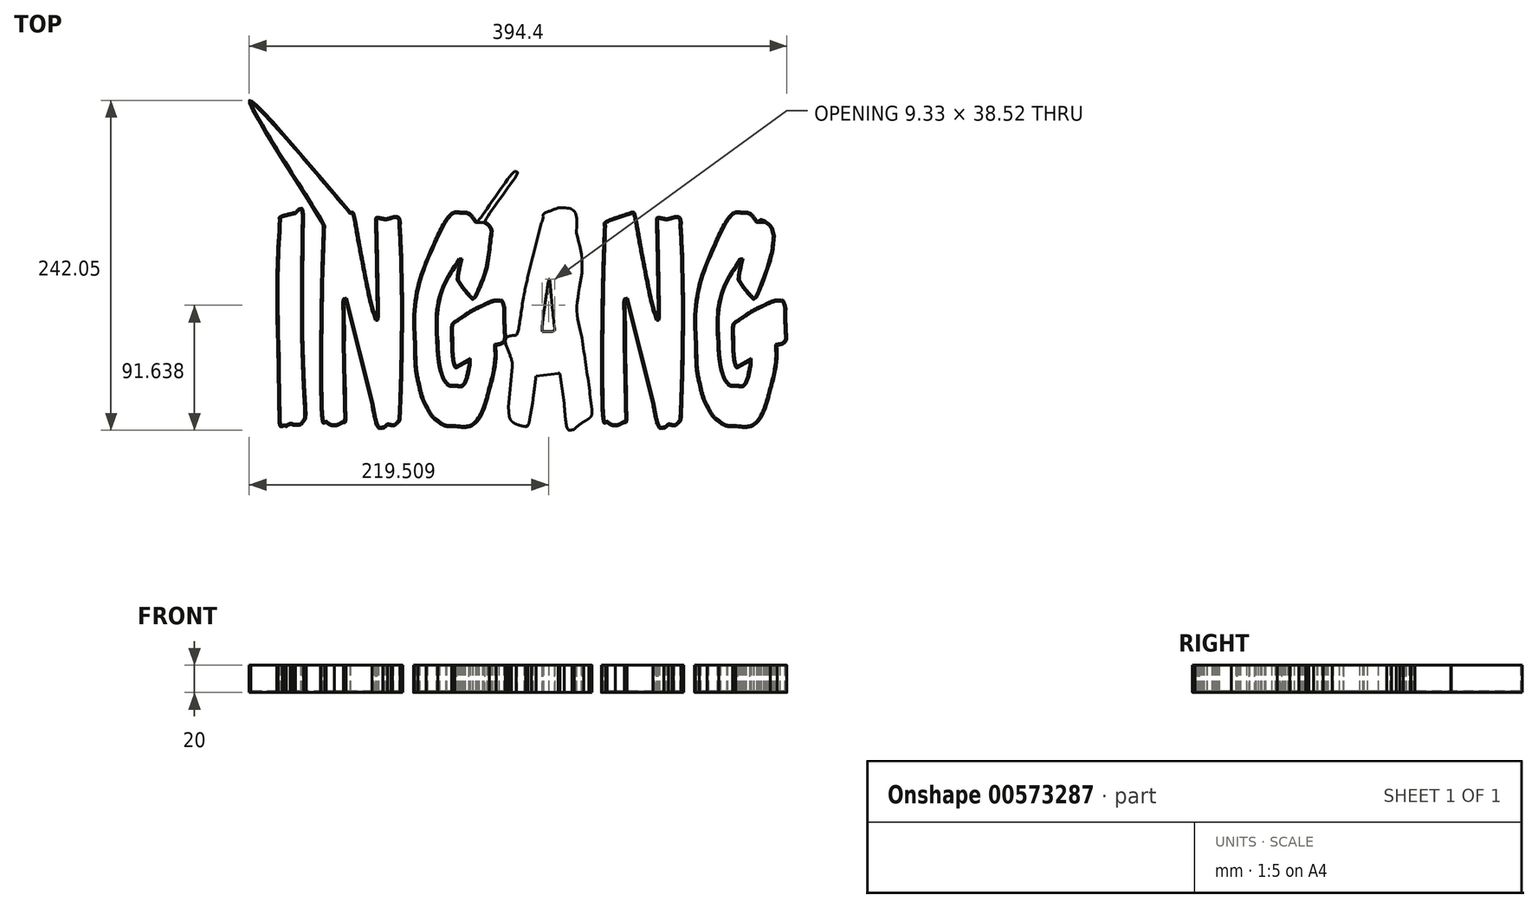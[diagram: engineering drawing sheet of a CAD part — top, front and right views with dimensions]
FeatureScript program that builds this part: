
annotation { "Feature Type Name" : "Feature", "Feature Type Description" : "" }
export const myFeature = defineFeature(function(context is Context, id is Id, definition is map)
    precondition{}
    {
        {
            var Q0;
            Q0=qCreatedBy(makeId("Top.planeOp"),FACE);
            var sketch = newSketch(context, id + "F0", { "sketchPlane" : qUnion([Q0])});
            skFitSpline(sketch, "E0", {"points": [v(-169.64, 100.47) * mm, v(-168.45, 100.47) * mm, v(-167.69, 98.57) * mm, v(-167.37, 94.75) * mm]});
            skFitSpline(sketch, "E1", {"points": [v(-167.37, 94.75) * mm, v(-167.69, 74.14) * mm, v(-167.89, 56.43) * mm, v(-167.97, 41.62) * mm]});
            skFitSpline(sketch, "E2", {"points": [v(-167.97, 41.62) * mm, v(-168.05, 26.8) * mm, v(-168, 14.37) * mm, v(-167.85, 4.29) * mm]});
            skFitSpline(sketch, "E3", {"points": [v(-167.85, 4.29) * mm, v(-167.69, -2.12) * mm, v(-167.45, -9.53) * mm, v(-167.13, -17.92) * mm]});
            skFitSpline(sketch, "E4", {"points": [v(-167.13, -17.92) * mm, v(-166.8, -26.32) * mm, v(-166.33, -35.86) * mm, v(-165.7, -46.55) * mm]});
            skFitSpline(sketch, "E5", {"points": [v(-165.7, -46.55) * mm, v(-165.61, -51.28) * mm, v(-166.21, -54.5) * mm, v(-167.49, -56.17) * mm]});
            skFitSpline(sketch, "E6", {"points": [v(-167.49, -56.17) * mm, v(-168.76, -57.85) * mm, v(-170.72, -58.69) * mm, v(-173.36, -58.69) * mm]});
            skFitSpline(sketch, "E7", {"points": [v(-173.36, -58.69) * mm, v(-174.15, -58.69) * mm, v(-174.87, -58.61) * mm, v(-175.51, -58.46) * mm]});
            skFitSpline(sketch, "E8", {"points": [v(-175.51, -58.46) * mm, v(-176.15, -58.15) * mm, v(-176.7, -58.08) * mm, v(-177.19, -58.23) * mm]});
            skFitSpline(sketch, "E9", {"points": [v(-177.19, -58.23) * mm, v(-177.59, -58.23) * mm, v(-178.5, -58.69) * mm, v(-179.94, -59.6) * mm]});
            skFitSpline(sketch, "E10", {"points": [v(-182.94, -59.6) * mm, v(-184.53, -59.6) * mm, v(-185.45, -54.41) * mm, v(-185.7, -44.03) * mm]});
            skLineSegment(sketch, "E11", {"start": v(-179.94, -59.6) * mm, "end": v(-181.38, -59.15) * mm});
            skLineSegment(sketch, "E12", {"start": v(-181.38, -59.15) * mm, "end": v(-182.94, -59.6) * mm});
            skFitSpline(sketch, "E13", {"points": [v(-186.17, -11.74) * mm, v(-187.05, 27.95) * mm, v(-186.69, 62.69) * mm, v(-185.1, 92.46) * mm]});
            skFitSpline(sketch, "E14", {"points": [v(-185.1, 92.46) * mm, v(-185.25, 93.99) * mm, v(-181.38, 95.74) * mm, v(-173.48, 97.73) * mm]});
            skFitSpline(sketch, "E15", {"points": [v(-173.48, 97.73) * mm, v(-171.72, 99.56) * mm, v(-170.44, 100.47) * mm, v(-169.64, 100.47) * mm]});
            skLineSegment(sketch, "E16", {"start": v(-185.7, -44.03) * mm, "end": v(-186.17, -11.74) * mm});
            skFitSpline(sketch, "E17", {"points": [v(-132.92, 97.73) * mm, v(-131.25, 97.73) * mm, v(-128.53, 87.42) * mm, v(-124.78, 66.8) * mm]});
            skFitSpline(sketch, "E18", {"points": [v(-124.78, 66.8) * mm, v(-120.07, 42.69) * mm, v(-116.43, 26.89) * mm, v(-113.88, 19.4) * mm]});
            skFitSpline(sketch, "E19", {"points": [v(-113.64, 19.4) * mm, v(-113.48, 23.98) * mm, v(-113.48, 30.1) * mm, v(-113.64, 37.72) * mm]});
            skFitSpline(sketch, "E20", {"points": [v(-113.64, 37.72) * mm, v(-113.72, 42.46) * mm, v(-113.84, 49.18) * mm, v(-114, 57.88) * mm]});
            skFitSpline(sketch, "E21", {"points": [v(-114, 57.88) * mm, v(-114.16, 66.73) * mm, v(-114.4, 77.88) * mm, v(-114.72, 91.31) * mm]});
            skFitSpline(sketch, "E22", {"points": [v(-114.72, 91.31) * mm, v(-114.64, 93.15) * mm, v(-113.84, 94.06) * mm, v(-112.32, 94.06) * mm]});
            skFitSpline(sketch, "E23", {"points": [v(-112.32, 94.06) * mm, v(-110.97, 93.76) * mm, v(-109.93, 93.53) * mm, v(-109.2, 93.37) * mm]});
            skFitSpline(sketch, "E24", {"points": [v(-109.2, 93.37) * mm, v(-108.41, 93.22) * mm, v(-107.93, 93.15) * mm, v(-107.77, 93.15) * mm]});
            skLineSegment(sketch, "E25", {"start": v(-113.88, 19.4) * mm, "end": v(-113.64, 19.4) * mm});
            skFitSpline(sketch, "E26", {"points": [v(-107.05, 93.15) * mm, v(-106.57, 93.15) * mm, v(-104.82, 93.6) * mm, v(-101.78, 94.52) * mm]});
            skFitSpline(sketch, "E27", {"points": [v(-101.78, 94.52) * mm, v(-98.35, 94.52) * mm, v(-96.6, 92.15) * mm, v(-96.51, 87.42) * mm]});
            skFitSpline(sketch, "E28", {"points": [v(-96.51, 87.42) * mm, v(-96.2, 83.15) * mm, v(-95.96, 78.72) * mm, v(-95.8, 74.14) * mm]});
            skFitSpline(sketch, "E29", {"points": [v(-95.8, 74.14) * mm, v(-95.56, 69.71) * mm, v(-95.36, 65.13) * mm, v(-95.2, 60.4) * mm]});
            skLineSegment(sketch, "E30", {"start": v(-107.77, 93.15) * mm, "end": v(-107.05, 93.15) * mm});
            skFitSpline(sketch, "E31", {"points": [v(-94.96, 45.74) * mm, v(-94.72, 31.85) * mm, v(-94.72, 16.58) * mm, v(-94.96, -0.06) * mm]});
            skFitSpline(sketch, "E32", {"points": [v(-94.96, -0.06) * mm, v(-95.2, -16.55) * mm, v(-95.72, -34.8) * mm, v(-96.51, -54.8) * mm]});
            skFitSpline(sketch, "E33", {"points": [v(-96.51, -54.8) * mm, v(-98.83, -57.54) * mm, v(-100.7, -58.92) * mm, v(-102.14, -58.92) * mm]});
            skLineSegment(sketch, "E34", {"start": v(-95.2, 60.4) * mm, "end": v(-94.96, 45.74) * mm});
            skFitSpline(sketch, "E35", {"points": [v(-103.34, -58.92) * mm, v(-103.9, -58.76) * mm, v(-104.7, -58.61) * mm, v(-105.74, -58.46) * mm]});
            skFitSpline(sketch, "E36", {"points": [v(-105.74, -58.46) * mm, v(-107.41, -59.99) * mm, v(-108.57, -60.75) * mm, v(-109.2, -60.75) * mm]});
            skFitSpline(sketch, "E37", {"points": [v(-109.2, -60.75) * mm, v(-112.32, -60.75) * mm, v(-115.04, -55.1) * mm, v(-117.35, -43.8) * mm]});
            skLineSegment(sketch, "E38", {"start": v(-102.14, -58.92) * mm, "end": v(-103.34, -58.92) * mm});
            skFitSpline(sketch, "E39", {"points": [v(-136.87, 33.6) * mm, v(-137.35, 33.6) * mm, v(-137.51, 23.07) * mm, v(-137.35, 2) * mm]});
            skLineSegment(sketch, "E40", {"start": v(-117.35, -43.8) * mm, "end": v(-136.63, 33.6) * mm});
            skLineSegment(sketch, "E41", {"start": v(-136.63, 33.6) * mm, "end": v(-136.87, 33.6) * mm});
            skFitSpline(sketch, "E42", {"points": [v(-136.75, -28.46) * mm, v(-136.43, -47.24) * mm, v(-136.95, -56.63) * mm, v(-138.31, -56.63) * mm]});
            skFitSpline(sketch, "E43", {"points": [v(-138.31, -56.63) * mm, v(-141.03, -58.15) * mm, v(-143.18, -58.92) * mm, v(-144.78, -58.92) * mm]});
            skFitSpline(sketch, "E44", {"points": [v(-144.78, -58.92) * mm, v(-146.93, -58.92) * mm, v(-148.93, -58.15) * mm, v(-150.77, -56.63) * mm]});
            skLineSegment(sketch, "E45", {"start": v(-137.35, 2) * mm, "end": v(-136.75, -28.46) * mm});
            skFitSpline(sketch, "E46", {"points": [v(-151.72, -57.09) * mm, v(-153.08, -57.09) * mm, v(-154.04, -53.65) * mm, v(-154.6, -46.78) * mm]});
            skFitSpline(sketch, "E47", {"points": [v(-154.6, -46.78) * mm, v(-155, -25.1) * mm, v(-155.04, -3.34) * mm, v(-154.72, 18.49) * mm]});
            skFitSpline(sketch, "E48", {"points": [v(-154.72, 18.49) * mm, v(-154.4, 40.47) * mm, v(-153.8, 63.45) * mm, v(-152.92, 87.42) * mm]});
            skFitSpline(sketch, "E49", {"points": [v(-152.92, 87.42) * mm, v(-153.43, 89.02) * mm, v(-207.01, 177.85) * mm, v(-132.92, 97.73) * mm]});
            skLineSegment(sketch, "E50", {"start": v(-150.77, -56.63) * mm, "end": v(-151.72, -57.09) * mm});
            skFitSpline(sketch, "E51", {"points": [v(-50.81, 97.73) * mm, v(-47.46, 97.73) * mm, v(-44.15, 95.51) * mm, v(-40.87, 91.08) * mm]});
            skFitSpline(sketch, "E52", {"points": [v(-40.4, 91.08) * mm, v(-38.96, 92) * mm, v(-12.73, 127.61) * mm, v(-11.56, 127.23) * mm]});
            skFitSpline(sketch, "E53", {"points": [v(-11.56, 127.23) * mm, v(-10.4, 126.85) * mm, v(-34.2, 90.86) * mm, v(-33.09, 89.94) * mm]});
            skFitSpline(sketch, "E54", {"points": [v(-33.09, 89.94) * mm, v(-31.9, 89.18) * mm, v(-30.97, 88.26) * mm, v(-30.33, 87.2) * mm]});
            skFitSpline(sketch, "E55", {"points": [v(-30.33, 87.2) * mm, v(-29.7, 86.28) * mm, v(-29.26, 85.2) * mm, v(-29.02, 83.99) * mm]});
            skFitSpline(sketch, "E56", {"points": [v(-29.02, 83.99) * mm, v(-30.3, 73.15) * mm, v(-32.93, 56.12) * mm, v(-38.84, 40.24) * mm]});
            skFitSpline(sketch, "E57", {"points": [v(-38.84, 40.24) * mm, v(-40.35, 36.89) * mm, v(-41.8, 34.75) * mm, v(-43.15, 33.83) * mm]});
            skFitSpline(sketch, "E58", {"points": [v(-43.15, 33.83) * mm, v(-43.63, 33.83) * mm, v(-44.5, 34.52) * mm, v(-45.78, 35.9) * mm]});
            skFitSpline(sketch, "E59", {"points": [v(-45.78, 35.9) * mm, v(-47.06, 37.27) * mm, v(-48.38, 38.8) * mm, v(-49.73, 40.47) * mm]});
            skFitSpline(sketch, "E60", {"points": [v(-49.73, 40.47) * mm, v(-51.1, 42.15) * mm, v(-52.29, 43.83) * mm, v(-53.33, 45.51) * mm]});
            skFitSpline(sketch, "E61", {"points": [v(-53.33, 45.51) * mm, v(-54.37, 47.2) * mm, v(-54.88, 48.26) * mm, v(-54.88, 48.72) * mm]});
            skFitSpline(sketch, "E62", {"points": [v(-54.88, 48.72) * mm, v(-54.57, 51.92) * mm, v(-53.73, 56.5) * mm, v(-52.37, 62.46) * mm]});
            skLineSegment(sketch, "E63", {"start": v(-40.87, 91.08) * mm, "end": v(-40.4, 91.08) * mm});
            skFitSpline(sketch, "E64", {"points": [v(-52.85, 62.46) * mm, v(-63.79, 44.29) * mm, v(-69.02, 23.3) * mm, v(-68.54, -0.52) * mm]});
            skFitSpline(sketch, "E65", {"points": [v(-68.54, -0.52) * mm, v(-68.46, -4.18) * mm, v(-68.18, -7.77) * mm, v(-67.7, -11.28) * mm]});
            skFitSpline(sketch, "E66", {"points": [v(-67.7, -11.28) * mm, v(-67.22, -14.64) * mm, v(-66.58, -17.7) * mm, v(-65.78, -20.44) * mm]});
            skFitSpline(sketch, "E67", {"points": [v(-65.78, -20.44) * mm, v(-64.9, -23.04) * mm, v(-63.83, -25.18) * mm, v(-62.55, -26.86) * mm]});
            skFitSpline(sketch, "E68", {"points": [v(-62.55, -26.86) * mm, v(-61.27, -28.38) * mm, v(-59.75, -29.15) * mm, v(-58, -29.15) * mm]});
            skLineSegment(sketch, "E69", {"start": v(-52.37, 62.46) * mm, "end": v(-52.85, 62.46) * mm});
            skFitSpline(sketch, "E70", {"points": [v(-54.88, -29.15) * mm, v(-51.3, -29.15) * mm, v(-48.5, -24.72) * mm, v(-46.5, -15.86) * mm]});
            skFitSpline(sketch, "E71", {"points": [v(-46.5, -15.86) * mm, v(-46.18, -14.8) * mm, v(-46.02, -13.57) * mm, v(-46.02, -12.2) * mm]});
            skLineSegment(sketch, "E72", {"start": v(-58, -29.15) * mm, "end": v(-54.88, -29.15) * mm});
            skFitSpline(sketch, "E73", {"points": [v(-55.36, -16.32) * mm, v(-56.16, -16.32) * mm, v(-56.8, -15.56) * mm, v(-57.28, -14.03) * mm]});
            skFitSpline(sketch, "E74", {"points": [v(-57.28, -14.03) * mm, v(-57.76, -12.5) * mm, v(-58.12, -10.67) * mm, v(-58.36, -8.54) * mm]});
            skFitSpline(sketch, "E75", {"points": [v(-58.36, -8.54) * mm, v(-58.6, -6.25) * mm, v(-58.76, -3.8) * mm, v(-58.84, -1.2) * mm]});
            skFitSpline(sketch, "E76", {"points": [v(-58.84, -1.2) * mm, v(-58.92, 1.39) * mm, v(-58.96, 3.83) * mm, v(-58.96, 6.12) * mm]});
            skFitSpline(sketch, "E77", {"points": [v(-58.96, 6.12) * mm, v(-59.12, 12.53) * mm, v(-58.04, 16.58) * mm, v(-55.72, 18.26) * mm]});
            skFitSpline(sketch, "E78", {"points": [v(-55.72, 18.26) * mm, v(-47.98, 23.45) * mm, v(-41.51, 27.27) * mm, v(-36.32, 29.7) * mm]});
            skFitSpline(sketch, "E79", {"points": [v(-36.32, 29.7) * mm, v(-31.05, 32.15) * mm, v(-27.02, 33.37) * mm, v(-24.23, 33.37) * mm]});
            skFitSpline(sketch, "E80", {"points": [v(-24.23, 33.37) * mm, v(-22.23, 33.37) * mm, v(-20.67, 31.16) * mm, v(-19.56, 26.73) * mm]});
            skFitSpline(sketch, "E81", {"points": [v(-19.56, 26.73) * mm, v(-19.64, 25.51) * mm, v(-19.71, 24.37) * mm, v(-19.8, 23.3) * mm]});
            skFitSpline(sketch, "E82", {"points": [v(-19.8, 23.3) * mm, v(-19.8, 22.38) * mm, v(-19.75, 21.62) * mm, v(-19.68, 21) * mm]});
            skFitSpline(sketch, "E83", {"points": [v(-19.68, 21) * mm, v(-19.68, 19.48) * mm, v(-19.63, 17.72) * mm, v(-19.56, 15.74) * mm]});
            skFitSpline(sketch, "E84", {"points": [v(-19.56, 15.74) * mm, v(-19.4, 13.9) * mm, v(-19.32, 11.77) * mm, v(-19.32, 9.33) * mm]});
            skFitSpline(sketch, "E85", {"points": [v(-19.32, 9.33) * mm, v(-19.16, 4.44) * mm, v(-21.51, 1.31) * mm, v(-26.38, -0.06) * mm]});
            skFitSpline(sketch, "E86", {"points": [v(-26.38, -0.06) * mm, v(-26.22, -9.53) * mm, v(-27.82, -20.75) * mm, v(-31.17, -33.73) * mm]});
            skFitSpline(sketch, "E87", {"points": [v(-31.17, -33.73) * mm, v(-36.84, -50.98) * mm, v(-45.26, -59.6) * mm, v(-56.44, -59.6) * mm]});
            skLineSegment(sketch, "E88", {"start": v(-46.02, -12.2) * mm, "end": v(-46.02, -11.28) * mm});
            skLineSegment(sketch, "E89", {"start": v(-46.02, -11.28) * mm, "end": v(-55.36, -16.32) * mm});
            skFitSpline(sketch, "E90", {"points": [v(-58.72, -59.6) * mm, v(-62.3, -59.6) * mm, v(-65.7, -58.46) * mm, v(-68.9, -56.17) * mm]});
            skFitSpline(sketch, "E91", {"points": [v(-68.9, -56.17) * mm, v(-72.1, -53.73) * mm, v(-74.92, -50.22) * mm, v(-77.4, -45.64) * mm]});
            skFitSpline(sketch, "E92", {"points": [v(-77.4, -45.64) * mm, v(-79.8, -41.05) * mm, v(-81.8, -35.33) * mm, v(-83.39, -28.46) * mm]});
            skFitSpline(sketch, "E93", {"points": [v(-83.39, -28.46) * mm, v(-84.9, -21.44) * mm, v(-85.78, -13.34) * mm, v(-86.02, -4.18) * mm]});
            skLineSegment(sketch, "E94", {"start": v(-56.44, -59.6) * mm, "end": v(-58.72, -59.6) * mm});
            skFitSpline(sketch, "E95", {"points": [v(-86.02, -1.44) * mm, v(-86.5, 24.98) * mm, v(-81.91, 50.17) * mm, v(-72.25, 74.14) * mm]});
            skFitSpline(sketch, "E96", {"points": [v(-72.25, 74.14) * mm, v(-64.59, 89.86) * mm, v(-57.6, 97.73) * mm, v(-51.3, 97.73) * mm]});
            skLineSegment(sketch, "E97", {"start": v(-86.02, -4.18) * mm, "end": v(-86.02, -1.44) * mm});
            skFitSpline(sketch, "E98", {"points": [v(19.36, 100.93) * mm, v(20.96, 100.93) * mm, v(30.4, 99.19) * mm, v(32.63, 82.55) * mm]});
            skFitSpline(sketch, "E99", {"points": [v(32.63, 82.55) * mm, v(36.94, 57.66) * mm, v(33.13, 28.49) * mm, v(36.25, 8.18) * mm]});
            skFitSpline(sketch, "E100", {"points": [v(36.25, 8.18) * mm, v(39.36, -11.97) * mm, v(41.95, -30.37) * mm, v(44.03, -47) * mm]});
            skLineSegment(sketch, "E101", {"start": v(-51.3, 97.73) * mm, "end": v(-50.81, 97.73) * mm});
            skFitSpline(sketch, "E102", {"points": [v(44.03, -47.93) * mm, v(44.1, -49.6) * mm, v(44, -50.83) * mm, v(43.67, -51.59) * mm]});
            skFitSpline(sketch, "E103", {"points": [v(43.67, -51.59) * mm, v(43.43, -52.2) * mm, v(42.83, -52.89) * mm, v(41.87, -53.65) * mm]});
            skFitSpline(sketch, "E104", {"points": [v(41.87, -53.65) * mm, v(41, -54.26) * mm, v(39.68, -55.1) * mm, v(37.92, -56.17) * mm]});
            skFitSpline(sketch, "E105", {"points": [v(37.92, -56.17) * mm, v(36.17, -57.24) * mm, v(33.9, -59) * mm, v(31.1, -61.44) * mm]});
            skFitSpline(sketch, "E106", {"points": [v(31.1, -61.44) * mm, v(30.94, -61.74) * mm, v(30.38, -61.9) * mm, v(29.42, -61.9) * mm]});
            skFitSpline(sketch, "E107", {"points": [v(29.42, -61.9) * mm, v(26.78, -61.9) * mm, v(24.87, -55.48) * mm, v(23.67, -42.66) * mm]});
            skLineSegment(sketch, "E108", {"start": v(44.03, -47) * mm, "end": v(44.03, -47.93) * mm});
            skFitSpline(sketch, "E109", {"points": [v(20.56, -20.67) * mm, v(20.24, -20.67) * mm, v(20.08, -20.52) * mm, v(20.08, -20.21) * mm]});
            skFitSpline(sketch, "E110", {"points": [v(20.08, -20.21) * mm, v(20, -20.37) * mm, v(19.8, -20.44) * mm, v(19.48, -20.44) * mm]});
            skFitSpline(sketch, "E111", {"points": [v(19.48, -20.44) * mm, v(19.4, -20.44) * mm, v(19.36, -20.52) * mm, v(19.36, -20.67) * mm]});
            skLineSegment(sketch, "E112", {"start": v(23.67, -42.66) * mm, "end": v(20.56, -20.67) * mm});
            skFitSpline(sketch, "E113", {"points": [v(3.07, -22.5) * mm, v(1.71, -33.5) * mm, v(0.52, -41.97) * mm, v(-0.52, -47.93) * mm]});
            skFitSpline(sketch, "E114", {"points": [v(-0.52, -47.93) * mm, v(-1.48, -53.88) * mm, v(-2.24, -57.47) * mm, v(-2.8, -58.69) * mm]});
            skLineSegment(sketch, "E115", {"start": v(19.36, -20.67) * mm, "end": v(3.07, -22.5) * mm});
            skFitSpline(sketch, "E116", {"points": [v(-4.47, -59.6) * mm, v(-7.43, -59) * mm, v(-9.74, -58.38) * mm, v(-11.42, -57.77) * mm]});
            skFitSpline(sketch, "E117", {"points": [v(-11.42, -57.77) * mm, v(-13.02, -57) * mm, v(-14.21, -56.17) * mm, v(-15.01, -55.25) * mm]});
            skFitSpline(sketch, "E118", {"points": [v(-15.01, -55.25) * mm, v(-15.81, -54.18) * mm, v(-16.33, -52.89) * mm, v(-16.57, -51.36) * mm]});
            skFitSpline(sketch, "E119", {"points": [v(-16.57, -51.36) * mm, v(-16.8, -49.83) * mm, v(-16.97, -47.85) * mm, v(-17.05, -45.4) * mm]});
            skLineSegment(sketch, "E120", {"start": v(-2.8, -58.69) * mm, "end": v(-4.47, -59.6) * mm});
            skFitSpline(sketch, "E121", {"points": [v(-14.41, -15.4) * mm, v(-14.41, -12.66) * mm, v(-15.9, -7.54) * mm, v(-18.84, -0.06) * mm]});
            skFitSpline(sketch, "E122", {"points": [v(-18.84, -0.06) * mm, v(-18.92, 0.1) * mm, v(-18.96, 0.4) * mm, v(-18.96, 0.85) * mm]});
            skFitSpline(sketch, "E123", {"points": [v(-18.96, 0.85) * mm, v(-18.96, 1) * mm, v(-19, 1.16) * mm, v(-19.08, 1.31) * mm]});
            skFitSpline(sketch, "E124", {"points": [v(-19.08, 1.31) * mm, v(-19.24, 4.67) * mm, v(-16.73, 6.73) * mm, v(-11.54, 7.5) * mm]});
            skFitSpline(sketch, "E125", {"points": [v(-11.54, 7.5) * mm, v(-10.58, 8.87) * mm, v(-8.66, 18.72) * mm, v(-5.8, 37.04) * mm]});
            skFitSpline(sketch, "E126", {"points": [v(-5.8, 37.04) * mm, v(-3.71, 46.8) * mm, v(-1.48, 56.43) * mm, v(0.92, 65.9) * mm]});
            skFitSpline(sketch, "E127", {"points": [v(0.92, 65.9) * mm, v(3.31, 75.51) * mm, v(5.83, 85.13) * mm, v(8.46, 94.75) * mm]});
            skFitSpline(sketch, "E128", {"points": [v(8.46, 94.75) * mm, v(8.38, 96.12) * mm, v(12.01, 98.18) * mm, v(19.36, 100.93) * mm]});
            skLineSegment(sketch, "E129", {"start": v(-17.05, -45.4) * mm, "end": v(-14.41, -15.4) * mm});
            skFitSpline(sketch, "E130", {"points": [v(12.41, 48.72) * mm, v(10.82, 38.18) * mm, v(9.58, 29.7) * mm, v(8.7, 23.3) * mm]});
            skFitSpline(sketch, "E131", {"points": [v(8.7, 23.3) * mm, v(7.9, 16.88) * mm, v(7.54, 12.53) * mm, v(7.62, 10.24) * mm]});
            skFitSpline(sketch, "E132", {"points": [v(7.62, 10.24) * mm, v(13.7, 10.24) * mm, v(16.72, 10.93) * mm, v(16.72, 12.3) * mm]});
            skFitSpline(sketch, "E133", {"points": [v(16.72, 12.3) * mm, v(14.17, 36.58) * mm, v(12.73, 48.72) * mm, v(12.41, 48.72) * mm]});
            skFitSpline(sketch, "E134", {"points": [v(73.15, 97.73) * mm, v(74.83, 97.73) * mm, v(77.54, 87.42) * mm, v(81.3, 66.8) * mm]});
            skFitSpline(sketch, "E135", {"points": [v(81.3, 66.8) * mm, v(86, 42.69) * mm, v(89.64, 26.89) * mm, v(92.2, 19.4) * mm]});
            skFitSpline(sketch, "E136", {"points": [v(92.43, 19.4) * mm, v(92.6, 23.98) * mm, v(92.6, 30.1) * mm, v(92.43, 37.72) * mm]});
            skFitSpline(sketch, "E137", {"points": [v(92.43, 37.72) * mm, v(92.35, 42.46) * mm, v(92.23, 49.18) * mm, v(92.07, 57.88) * mm]});
            skFitSpline(sketch, "E138", {"points": [v(92.07, 57.88) * mm, v(91.91, 66.73) * mm, v(91.67, 77.88) * mm, v(91.35, 91.31) * mm]});
            skFitSpline(sketch, "E139", {"points": [v(91.35, 91.31) * mm, v(91.43, 93.15) * mm, v(92.23, 94.06) * mm, v(93.75, 94.06) * mm]});
            skFitSpline(sketch, "E140", {"points": [v(93.75, 94.06) * mm, v(95.1, 93.76) * mm, v(96.14, 93.53) * mm, v(96.86, 93.37) * mm]});
            skFitSpline(sketch, "E141", {"points": [v(96.86, 93.37) * mm, v(97.66, 93.22) * mm, v(98.14, 93.15) * mm, v(98.3, 93.15) * mm]});
            skLineSegment(sketch, "E142", {"start": v(92.2, 19.4) * mm, "end": v(92.43, 19.4) * mm});
            skFitSpline(sketch, "E143", {"points": [v(99.02, 93.15) * mm, v(99.5, 93.15) * mm, v(101.25, 93.6) * mm, v(104.29, 94.52) * mm]});
            skFitSpline(sketch, "E144", {"points": [v(104.29, 94.52) * mm, v(107.72, 94.52) * mm, v(109.48, 92.15) * mm, v(109.56, 87.42) * mm]});
            skFitSpline(sketch, "E145", {"points": [v(109.56, 87.42) * mm, v(109.88, 83.15) * mm, v(110.12, 78.72) * mm, v(110.28, 74.14) * mm]});
            skFitSpline(sketch, "E146", {"points": [v(110.28, 74.14) * mm, v(110.52, 69.71) * mm, v(110.72, 65.13) * mm, v(110.88, 60.4) * mm]});
            skLineSegment(sketch, "E147", {"start": v(98.3, 93.15) * mm, "end": v(99.02, 93.15) * mm});
            skFitSpline(sketch, "E148", {"points": [v(111.11, 45.74) * mm, v(111.35, 31.85) * mm, v(111.35, 16.58) * mm, v(111.11, -0.06) * mm]});
            skFitSpline(sketch, "E149", {"points": [v(111.11, -0.06) * mm, v(110.88, -16.55) * mm, v(110.36, -34.8) * mm, v(109.56, -54.8) * mm]});
            skFitSpline(sketch, "E150", {"points": [v(109.56, -54.8) * mm, v(107.24, -57.54) * mm, v(105.37, -58.92) * mm, v(103.93, -58.92) * mm]});
            skLineSegment(sketch, "E151", {"start": v(110.88, 60.4) * mm, "end": v(111.11, 45.74) * mm});
            skFitSpline(sketch, "E152", {"points": [v(102.73, -58.92) * mm, v(102.17, -58.76) * mm, v(101.37, -58.61) * mm, v(100.34, -58.46) * mm]});
            skFitSpline(sketch, "E153", {"points": [v(100.34, -58.46) * mm, v(98.66, -59.99) * mm, v(97.5, -60.75) * mm, v(96.86, -60.75) * mm]});
            skFitSpline(sketch, "E154", {"points": [v(96.86, -60.75) * mm, v(93.75, -60.75) * mm, v(91.03, -55.1) * mm, v(88.72, -43.8) * mm]});
            skLineSegment(sketch, "E155", {"start": v(103.93, -58.92) * mm, "end": v(102.73, -58.92) * mm});
            skFitSpline(sketch, "E156", {"points": [v(69.2, 33.6) * mm, v(68.72, 33.6) * mm, v(68.56, 23.07) * mm, v(68.72, 2) * mm]});
            skLineSegment(sketch, "E157", {"start": v(88.72, -43.8) * mm, "end": v(69.44, 33.6) * mm});
            skLineSegment(sketch, "E158", {"start": v(69.44, 33.6) * mm, "end": v(69.2, 33.6) * mm});
            skFitSpline(sketch, "E159", {"points": [v(69.32, -28.46) * mm, v(69.64, -47.24) * mm, v(69.12, -56.63) * mm, v(67.76, -56.63) * mm]});
            skFitSpline(sketch, "E160", {"points": [v(67.76, -56.63) * mm, v(65.05, -58.15) * mm, v(62.9, -58.92) * mm, v(61.3, -58.92) * mm]});
            skFitSpline(sketch, "E161", {"points": [v(61.3, -58.92) * mm, v(59.14, -58.92) * mm, v(57.14, -58.15) * mm, v(55.3, -56.63) * mm]});
            skLineSegment(sketch, "E162", {"start": v(68.72, 2) * mm, "end": v(69.32, -28.46) * mm});
            skFitSpline(sketch, "E163", {"points": [v(54.35, -57.09) * mm, v(53, -57.09) * mm, v(52.03, -53.65) * mm, v(51.47, -46.78) * mm]});
            skFitSpline(sketch, "E164", {"points": [v(51.47, -46.78) * mm, v(51.07, -25.1) * mm, v(51.03, -3.34) * mm, v(51.35, 18.49) * mm]});
            skFitSpline(sketch, "E165", {"points": [v(51.35, 18.49) * mm, v(51.67, 40.47) * mm, v(52.27, 63.45) * mm, v(53.15, 87.42) * mm]});
            skFitSpline(sketch, "E166", {"points": [v(53.15, 87.42) * mm, v(53.15, 89.86) * mm, v(59.82, 93.3) * mm, v(73.15, 97.73) * mm]});
            skLineSegment(sketch, "E167", {"start": v(55.3, -56.63) * mm, "end": v(54.35, -57.09) * mm});
            skFitSpline(sketch, "E168", {"points": [v(155.26, 97.73) * mm, v(158.61, 97.73) * mm, v(161.93, 95.51) * mm, v(165.2, 91.08) * mm]});
            skFitSpline(sketch, "E169", {"points": [v(165.68, 91.08) * mm, v(167.12, 92) * mm, v(167.95, 92.46) * mm, v(168.2, 92.46) * mm]});
            skFitSpline(sketch, "E170", {"points": [v(168.2, 92.46) * mm, v(170.27, 91.7) * mm, v(171.87, 90.86) * mm, v(172.98, 89.94) * mm]});
            skFitSpline(sketch, "E171", {"points": [v(172.98, 89.94) * mm, v(174.18, 89.18) * mm, v(175.1, 88.26) * mm, v(175.74, 87.2) * mm]});
            skFitSpline(sketch, "E172", {"points": [v(175.74, 87.2) * mm, v(176.38, 86.28) * mm, v(176.82, 85.2) * mm, v(177.06, 83.99) * mm]});
            skFitSpline(sketch, "E173", {"points": [v(177.06, 83.99) * mm, v(177.38, 82.92) * mm, v(177.7, 81.7) * mm, v(178.01, 80.32) * mm]});
            skFitSpline(sketch, "E174", {"points": [v(178.01, 80.32) * mm, v(176.74, 69.48) * mm, v(173.14, 56.12) * mm, v(167.24, 40.24) * mm]});
            skFitSpline(sketch, "E175", {"points": [v(167.24, 40.24) * mm, v(165.72, 36.89) * mm, v(164.28, 34.75) * mm, v(162.92, 33.83) * mm]});
            skFitSpline(sketch, "E176", {"points": [v(162.92, 33.83) * mm, v(162.45, 33.83) * mm, v(161.57, 34.52) * mm, v(160.29, 35.9) * mm]});
            skFitSpline(sketch, "E177", {"points": [v(160.29, 35.9) * mm, v(159.01, 37.27) * mm, v(157.7, 38.8) * mm, v(156.34, 40.47) * mm]});
            skFitSpline(sketch, "E178", {"points": [v(156.34, 40.47) * mm, v(154.98, 42.15) * mm, v(153.78, 43.83) * mm, v(152.74, 45.51) * mm]});
            skFitSpline(sketch, "E179", {"points": [v(152.74, 45.51) * mm, v(151.7, 47.2) * mm, v(151.19, 48.26) * mm, v(151.19, 48.72) * mm]});
            skFitSpline(sketch, "E180", {"points": [v(151.19, 48.72) * mm, v(151.5, 51.92) * mm, v(152.35, 56.5) * mm, v(153.7, 62.46) * mm]});
            skLineSegment(sketch, "E181", {"start": v(165.2, 91.08) * mm, "end": v(165.68, 91.08) * mm});
            skFitSpline(sketch, "E182", {"points": [v(153.22, 62.46) * mm, v(142.29, 44.29) * mm, v(137.06, 23.3) * mm, v(137.53, -0.52) * mm]});
            skFitSpline(sketch, "E183", {"points": [v(137.53, -0.52) * mm, v(137.61, -4.18) * mm, v(137.9, -7.77) * mm, v(138.37, -11.28) * mm]});
            skFitSpline(sketch, "E184", {"points": [v(138.37, -11.28) * mm, v(138.85, -14.64) * mm, v(139.5, -17.7) * mm, v(140.29, -20.44) * mm]});
            skFitSpline(sketch, "E185", {"points": [v(140.29, -20.44) * mm, v(141.17, -23.04) * mm, v(142.25, -25.18) * mm, v(143.52, -26.86) * mm]});
            skFitSpline(sketch, "E186", {"points": [v(143.52, -26.86) * mm, v(144.8, -28.38) * mm, v(146.32, -29.15) * mm, v(148.07, -29.15) * mm]});
            skLineSegment(sketch, "E187", {"start": v(153.7, 62.46) * mm, "end": v(153.22, 62.46) * mm});
            skFitSpline(sketch, "E188", {"points": [v(151.19, -29.15) * mm, v(154.78, -29.15) * mm, v(157.57, -24.72) * mm, v(159.57, -15.86) * mm]});
            skFitSpline(sketch, "E189", {"points": [v(159.57, -15.86) * mm, v(159.9, -14.8) * mm, v(160.05, -13.57) * mm, v(160.05, -12.2) * mm]});
            skLineSegment(sketch, "E190", {"start": v(148.07, -29.15) * mm, "end": v(151.19, -29.15) * mm});
            skFitSpline(sketch, "E191", {"points": [v(150.7, -16.32) * mm, v(149.91, -16.32) * mm, v(149.27, -15.56) * mm, v(148.8, -14.03) * mm]});
            skFitSpline(sketch, "E192", {"points": [v(148.8, -14.03) * mm, v(148.31, -12.5) * mm, v(147.95, -10.67) * mm, v(147.71, -8.54) * mm]});
            skFitSpline(sketch, "E193", {"points": [v(147.71, -8.54) * mm, v(147.48, -6.25) * mm, v(147.32, -3.8) * mm, v(147.24, -1.2) * mm]});
            skFitSpline(sketch, "E194", {"points": [v(147.24, -1.2) * mm, v(147.16, 1.39) * mm, v(147.12, 3.83) * mm, v(147.12, 6.12) * mm]});
            skFitSpline(sketch, "E195", {"points": [v(147.12, 6.12) * mm, v(146.96, 12.53) * mm, v(148.03, 16.58) * mm, v(150.35, 18.26) * mm]});
            skFitSpline(sketch, "E196", {"points": [v(150.35, 18.26) * mm, v(158.1, 23.45) * mm, v(164.56, 27.27) * mm, v(169.75, 29.7) * mm]});
            skFitSpline(sketch, "E197", {"points": [v(169.75, 29.7) * mm, v(175.02, 32.15) * mm, v(179.05, 33.37) * mm, v(181.85, 33.37) * mm]});
            skFitSpline(sketch, "E198", {"points": [v(181.85, 33.37) * mm, v(183.84, 33.37) * mm, v(185.4, 31.16) * mm, v(186.52, 26.73) * mm]});
            skFitSpline(sketch, "E199", {"points": [v(186.52, 26.73) * mm, v(186.44, 25.51) * mm, v(186.36, 24.37) * mm, v(186.28, 23.3) * mm]});
            skFitSpline(sketch, "E200", {"points": [v(186.28, 23.3) * mm, v(186.28, 22.38) * mm, v(186.32, 21.62) * mm, v(186.4, 21) * mm]});
            skFitSpline(sketch, "E201", {"points": [v(186.4, 21) * mm, v(186.4, 19.48) * mm, v(186.43, 17.72) * mm, v(186.52, 15.74) * mm]});
            skFitSpline(sketch, "E202", {"points": [v(186.52, 15.74) * mm, v(186.68, 13.9) * mm, v(186.76, 11.77) * mm, v(186.76, 9.33) * mm]});
            skFitSpline(sketch, "E203", {"points": [v(186.76, 9.33) * mm, v(186.92, 4.44) * mm, v(184.56, 1.31) * mm, v(179.7, -0.06) * mm]});
            skFitSpline(sketch, "E204", {"points": [v(179.7, -0.06) * mm, v(179.85, -9.53) * mm, v(178.25, -20.75) * mm, v(174.9, -33.73) * mm]});
            skFitSpline(sketch, "E205", {"points": [v(174.9, -33.73) * mm, v(169.23, -50.98) * mm, v(160.8, -59.6) * mm, v(149.63, -59.6) * mm]});
            skLineSegment(sketch, "E206", {"start": v(160.05, -12.2) * mm, "end": v(160.05, -11.28) * mm});
            skLineSegment(sketch, "E207", {"start": v(160.05, -11.28) * mm, "end": v(150.7, -16.32) * mm});
            skFitSpline(sketch, "E208", {"points": [v(147.36, -59.6) * mm, v(143.76, -59.6) * mm, v(140.37, -58.46) * mm, v(137.18, -56.17) * mm]});
            skFitSpline(sketch, "E209", {"points": [v(137.18, -56.17) * mm, v(133.98, -53.73) * mm, v(131.15, -50.22) * mm, v(128.67, -45.64) * mm]});
            skFitSpline(sketch, "E210", {"points": [v(128.67, -45.64) * mm, v(126.28, -41.05) * mm, v(124.28, -35.33) * mm, v(122.68, -28.46) * mm]});
            skFitSpline(sketch, "E211", {"points": [v(122.68, -28.46) * mm, v(121.17, -21.44) * mm, v(120.29, -13.34) * mm, v(120.05, -4.18) * mm]});
            skLineSegment(sketch, "E212", {"start": v(149.63, -59.6) * mm, "end": v(147.36, -59.6) * mm});
            skFitSpline(sketch, "E213", {"points": [v(120.05, -1.44) * mm, v(119.57, 24.98) * mm, v(124.16, 50.17) * mm, v(133.82, 74.14) * mm]});
            skFitSpline(sketch, "E214", {"points": [v(133.82, 74.14) * mm, v(141.49, 89.86) * mm, v(148.47, 97.73) * mm, v(154.78, 97.73) * mm]});
            skLineSegment(sketch, "E215", {"start": v(120.05, -4.18) * mm, "end": v(120.05, -1.44) * mm});
            skLineSegment(sketch, "E216", {"start": v(154.78, 97.73) * mm, "end": v(155.26, 97.73) * mm});
            skSolve(sketch);
        }
        {
            var Q0;
            Q0=makeQuery(id+"F0.imprint","IMPRINT",FACE,{"disambiguationData":[TD([[makeQuery(id+"F0.imprint","IMPRINT",EDGE,{"derivedFrom":sQuery(id+"F0.wireOp",EDGE,"E98")}),-1.0]])]});
            var Q1;
            Q1=makeQuery(id+"F0.imprint","IMPRINT",FACE,{"disambiguationData":[TD([[makeQuery(id+"F0.imprint","IMPRINT",EDGE,{"derivedFrom":sQuery(id+"F0.wireOp",EDGE,"E134")}),-1.0]])]});
            var Q2;
            Q2=makeQuery(id+"F0.imprint","IMPRINT",FACE,{"disambiguationData":[TD([[makeQuery(id+"F0.imprint","IMPRINT",EDGE,{"derivedFrom":sQuery(id+"F0.wireOp",EDGE,"E168")}),-1.0]])]});
            var Q3;
            Q3=makeQuery(id+"F0.imprint","IMPRINT",FACE,{"disambiguationData":[TD([[makeQuery(id+"F0.imprint","IMPRINT",EDGE,{"derivedFrom":sQuery(id+"F0.wireOp",EDGE,"E51")}),-1.0]])]});
            var Q4;
            Q4=makeQuery(id+"F0.imprint","IMPRINT",FACE,{"disambiguationData":[TD([[makeQuery(id+"F0.imprint","IMPRINT",EDGE,{"derivedFrom":sQuery(id+"F0.wireOp",EDGE,"E17")}),-1.0]])]});
            var Q5;
            Q5=makeQuery(id+"F0.imprint","IMPRINT",FACE,{"disambiguationData":[TD([[makeQuery(id+"F0.imprint","IMPRINT",EDGE,{"derivedFrom":sQuery(id+"F0.wireOp",EDGE,"E0")}),-1.0]])]});
            extrude(context, id + "F1", {"entities" : qUnion([Q0, Q1, Q2, Q3, Q4, Q5]), "depth" : 20 * mm, "offsetDistance" : 25 * mm});
        }
        {
            var Q0;
            Q0=makeQuery(id+"F1.opExtrude","CAP_FACE",FACE,{"disambiguationData":[OSD([sQuery(id+"F0.wireOp",EDGE,"E0"),sQuery(id+"F0.wireOp",EDGE,"E1"),sQuery(id+"F0.wireOp",EDGE,"E2"),sQuery(id+"F0.wireOp",EDGE,"E3"),sQuery(id+"F0.wireOp",EDGE,"E4"),sQuery(id+"F0.wireOp",EDGE,"E5"),sQuery(id+"F0.wireOp",EDGE,"E6"),sQuery(id+"F0.wireOp",EDGE,"E7"),sQuery(id+"F0.wireOp",EDGE,"E8"),sQuery(id+"F0.wireOp",EDGE,"E9"),sQuery(id+"F0.wireOp",EDGE,"E10"),sQuery(id+"F0.wireOp",EDGE,"E11"),sQuery(id+"F0.wireOp",EDGE,"E12"),sQuery(id+"F0.wireOp",EDGE,"E13"),sQuery(id+"F0.wireOp",EDGE,"E14"),sQuery(id+"F0.wireOp",EDGE,"E15"),sQuery(id+"F0.wireOp",EDGE,"E16")])],"isStart":false});
            var Q1;
            Q1=makeQuery(id+"F1.opExtrude","CAP_FACE",FACE,{"disambiguationData":[OSD([sQuery(id+"F0.wireOp",EDGE,"E51"),sQuery(id+"F0.wireOp",EDGE,"E52"),sQuery(id+"F0.wireOp",EDGE,"E53"),sQuery(id+"F0.wireOp",EDGE,"E54"),sQuery(id+"F0.wireOp",EDGE,"E55"),sQuery(id+"F0.wireOp",EDGE,"E56"),sQuery(id+"F0.wireOp",EDGE,"E57"),sQuery(id+"F0.wireOp",EDGE,"E58"),sQuery(id+"F0.wireOp",EDGE,"E59"),sQuery(id+"F0.wireOp",EDGE,"E60"),sQuery(id+"F0.wireOp",EDGE,"E61"),sQuery(id+"F0.wireOp",EDGE,"E62"),sQuery(id+"F0.wireOp",EDGE,"E63"),sQuery(id+"F0.wireOp",EDGE,"E64"),sQuery(id+"F0.wireOp",EDGE,"E65"),sQuery(id+"F0.wireOp",EDGE,"E66"),sQuery(id+"F0.wireOp",EDGE,"E67"),sQuery(id+"F0.wireOp",EDGE,"E68"),sQuery(id+"F0.wireOp",EDGE,"E69"),sQuery(id+"F0.wireOp",EDGE,"E70"),sQuery(id+"F0.wireOp",EDGE,"E71"),sQuery(id+"F0.wireOp",EDGE,"E72"),sQuery(id+"F0.wireOp",EDGE,"E73"),sQuery(id+"F0.wireOp",EDGE,"E74"),sQuery(id+"F0.wireOp",EDGE,"E75"),sQuery(id+"F0.wireOp",EDGE,"E76"),sQuery(id+"F0.wireOp",EDGE,"E77"),sQuery(id+"F0.wireOp",EDGE,"E78"),sQuery(id+"F0.wireOp",EDGE,"E79"),sQuery(id+"F0.wireOp",EDGE,"E80"),sQuery(id+"F0.wireOp",EDGE,"E81"),sQuery(id+"F0.wireOp",EDGE,"E82"),sQuery(id+"F0.wireOp",EDGE,"E83"),sQuery(id+"F0.wireOp",EDGE,"E84"),sQuery(id+"F0.wireOp",EDGE,"E85"),sQuery(id+"F0.wireOp",EDGE,"E86"),sQuery(id+"F0.wireOp",EDGE,"E87"),sQuery(id+"F0.wireOp",EDGE,"E88"),sQuery(id+"F0.wireOp",EDGE,"E89"),sQuery(id+"F0.wireOp",EDGE,"E90"),sQuery(id+"F0.wireOp",EDGE,"E91"),sQuery(id+"F0.wireOp",EDGE,"E92"),sQuery(id+"F0.wireOp",EDGE,"E93"),sQuery(id+"F0.wireOp",EDGE,"E94"),sQuery(id+"F0.wireOp",EDGE,"E95"),sQuery(id+"F0.wireOp",EDGE,"E96"),sQuery(id+"F0.wireOp",EDGE,"E97"),sQuery(id+"F0.wireOp",EDGE,"E101")])],"isStart":false});
            var Q2;
            Q2=makeQuery(id+"F1.opExtrude","CAP_FACE",FACE,{"disambiguationData":[OSD([sQuery(id+"F0.wireOp",EDGE,"E134"),sQuery(id+"F0.wireOp",EDGE,"E135"),sQuery(id+"F0.wireOp",EDGE,"E136"),sQuery(id+"F0.wireOp",EDGE,"E137"),sQuery(id+"F0.wireOp",EDGE,"E138"),sQuery(id+"F0.wireOp",EDGE,"E139"),sQuery(id+"F0.wireOp",EDGE,"E140"),sQuery(id+"F0.wireOp",EDGE,"E141"),sQuery(id+"F0.wireOp",EDGE,"E142"),sQuery(id+"F0.wireOp",EDGE,"E143"),sQuery(id+"F0.wireOp",EDGE,"E144"),sQuery(id+"F0.wireOp",EDGE,"E145"),sQuery(id+"F0.wireOp",EDGE,"E146"),sQuery(id+"F0.wireOp",EDGE,"E147"),sQuery(id+"F0.wireOp",EDGE,"E148"),sQuery(id+"F0.wireOp",EDGE,"E149"),sQuery(id+"F0.wireOp",EDGE,"E150"),sQuery(id+"F0.wireOp",EDGE,"E151"),sQuery(id+"F0.wireOp",EDGE,"E152"),sQuery(id+"F0.wireOp",EDGE,"E153"),sQuery(id+"F0.wireOp",EDGE,"E154"),sQuery(id+"F0.wireOp",EDGE,"E155"),sQuery(id+"F0.wireOp",EDGE,"E156"),sQuery(id+"F0.wireOp",EDGE,"E157"),sQuery(id+"F0.wireOp",EDGE,"E158"),sQuery(id+"F0.wireOp",EDGE,"E159"),sQuery(id+"F0.wireOp",EDGE,"E160"),sQuery(id+"F0.wireOp",EDGE,"E161"),sQuery(id+"F0.wireOp",EDGE,"E162"),sQuery(id+"F0.wireOp",EDGE,"E163"),sQuery(id+"F0.wireOp",EDGE,"E164"),sQuery(id+"F0.wireOp",EDGE,"E165"),sQuery(id+"F0.wireOp",EDGE,"E166"),sQuery(id+"F0.wireOp",EDGE,"E167")])],"isStart":false});
            var Q3;
            Q3=makeQuery(id+"F1.opExtrude","CAP_FACE",FACE,{"disambiguationData":[OSD([sQuery(id+"F0.wireOp",EDGE,"E168"),sQuery(id+"F0.wireOp",EDGE,"E169"),sQuery(id+"F0.wireOp",EDGE,"E170"),sQuery(id+"F0.wireOp",EDGE,"E171"),sQuery(id+"F0.wireOp",EDGE,"E172"),sQuery(id+"F0.wireOp",EDGE,"E173"),sQuery(id+"F0.wireOp",EDGE,"E174"),sQuery(id+"F0.wireOp",EDGE,"E175"),sQuery(id+"F0.wireOp",EDGE,"E176"),sQuery(id+"F0.wireOp",EDGE,"E177"),sQuery(id+"F0.wireOp",EDGE,"E178"),sQuery(id+"F0.wireOp",EDGE,"E179"),sQuery(id+"F0.wireOp",EDGE,"E180"),sQuery(id+"F0.wireOp",EDGE,"E181"),sQuery(id+"F0.wireOp",EDGE,"E182"),sQuery(id+"F0.wireOp",EDGE,"E183"),sQuery(id+"F0.wireOp",EDGE,"E184"),sQuery(id+"F0.wireOp",EDGE,"E185"),sQuery(id+"F0.wireOp",EDGE,"E186"),sQuery(id+"F0.wireOp",EDGE,"E187"),sQuery(id+"F0.wireOp",EDGE,"E188"),sQuery(id+"F0.wireOp",EDGE,"E189"),sQuery(id+"F0.wireOp",EDGE,"E190"),sQuery(id+"F0.wireOp",EDGE,"E191"),sQuery(id+"F0.wireOp",EDGE,"E192"),sQuery(id+"F0.wireOp",EDGE,"E193"),sQuery(id+"F0.wireOp",EDGE,"E194"),sQuery(id+"F0.wireOp",EDGE,"E195"),sQuery(id+"F0.wireOp",EDGE,"E196"),sQuery(id+"F0.wireOp",EDGE,"E197"),sQuery(id+"F0.wireOp",EDGE,"E198"),sQuery(id+"F0.wireOp",EDGE,"E199"),sQuery(id+"F0.wireOp",EDGE,"E200"),sQuery(id+"F0.wireOp",EDGE,"E201"),sQuery(id+"F0.wireOp",EDGE,"E202"),sQuery(id+"F0.wireOp",EDGE,"E203"),sQuery(id+"F0.wireOp",EDGE,"E204"),sQuery(id+"F0.wireOp",EDGE,"E205"),sQuery(id+"F0.wireOp",EDGE,"E206"),sQuery(id+"F0.wireOp",EDGE,"E207"),sQuery(id+"F0.wireOp",EDGE,"E208"),sQuery(id+"F0.wireOp",EDGE,"E209"),sQuery(id+"F0.wireOp",EDGE,"E210"),sQuery(id+"F0.wireOp",EDGE,"E211"),sQuery(id+"F0.wireOp",EDGE,"E212"),sQuery(id+"F0.wireOp",EDGE,"E213"),sQuery(id+"F0.wireOp",EDGE,"E214"),sQuery(id+"F0.wireOp",EDGE,"E215"),sQuery(id+"F0.wireOp",EDGE,"E216")])],"isStart":false});
            var Q4;
            Q4=makeQuery(id+"F1.opExtrude","CAP_FACE",FACE,{"disambiguationData":[OSD([sQuery(id+"F0.wireOp",EDGE,"E17"),sQuery(id+"F0.wireOp",EDGE,"E18"),sQuery(id+"F0.wireOp",EDGE,"E19"),sQuery(id+"F0.wireOp",EDGE,"E20"),sQuery(id+"F0.wireOp",EDGE,"E21"),sQuery(id+"F0.wireOp",EDGE,"E22"),sQuery(id+"F0.wireOp",EDGE,"E23"),sQuery(id+"F0.wireOp",EDGE,"E24"),sQuery(id+"F0.wireOp",EDGE,"E25"),sQuery(id+"F0.wireOp",EDGE,"E26"),sQuery(id+"F0.wireOp",EDGE,"E27"),sQuery(id+"F0.wireOp",EDGE,"E28"),sQuery(id+"F0.wireOp",EDGE,"E29"),sQuery(id+"F0.wireOp",EDGE,"E30"),sQuery(id+"F0.wireOp",EDGE,"E31"),sQuery(id+"F0.wireOp",EDGE,"E32"),sQuery(id+"F0.wireOp",EDGE,"E33"),sQuery(id+"F0.wireOp",EDGE,"E34"),sQuery(id+"F0.wireOp",EDGE,"E35"),sQuery(id+"F0.wireOp",EDGE,"E36"),sQuery(id+"F0.wireOp",EDGE,"E37"),sQuery(id+"F0.wireOp",EDGE,"E38"),sQuery(id+"F0.wireOp",EDGE,"E39"),sQuery(id+"F0.wireOp",EDGE,"E40"),sQuery(id+"F0.wireOp",EDGE,"E41"),sQuery(id+"F0.wireOp",EDGE,"E42"),sQuery(id+"F0.wireOp",EDGE,"E43"),sQuery(id+"F0.wireOp",EDGE,"E44"),sQuery(id+"F0.wireOp",EDGE,"E45"),sQuery(id+"F0.wireOp",EDGE,"E46"),sQuery(id+"F0.wireOp",EDGE,"E47"),sQuery(id+"F0.wireOp",EDGE,"E48"),sQuery(id+"F0.wireOp",EDGE,"E49"),sQuery(id+"F0.wireOp",EDGE,"E50")])],"isStart":false});
            shell(context, id + "F2", {"entities" : qUnion([Q0, Q1, Q2, Q3, Q4]), "thickness" : 1 * mm});
        }
    });
